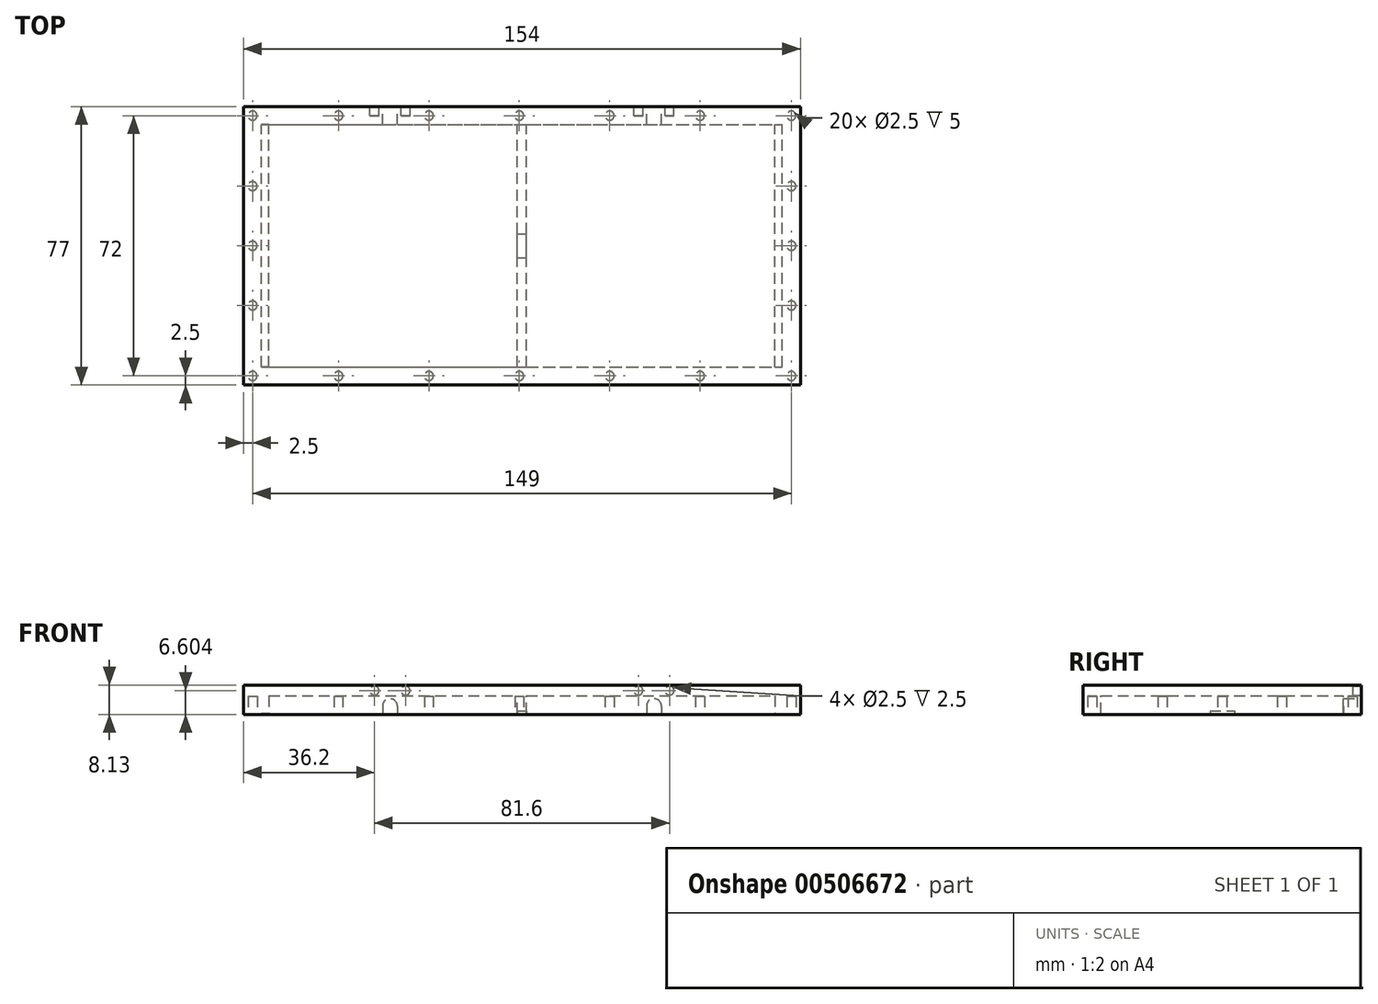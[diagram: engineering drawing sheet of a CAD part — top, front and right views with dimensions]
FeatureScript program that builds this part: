
annotation { "Feature Type Name" : "Feature", "Feature Type Description" : "" }
export const myFeature = defineFeature(function(context is Context, id is Id, definition is map)
    precondition{}
    {
        {
            var Q0;
            Q0=qCreatedBy(makeId("Top.planeOp"),FACE);
            var sketch = newSketch(context, id + "F0", { "sketchPlane" : qUnion([Q0])});
            skLineSegment(sketch, "E0.bottom", {"start": v(0, 0) * mm, "end": v(154, 0) * mm});
            skLineSegment(sketch, "E0.top", {"start": v(0, 77) * mm, "end": v(154, 77) * mm});
            skLineSegment(sketch, "E0.left", {"start": v(0, 0) * mm, "end": v(0, 77) * mm});
            skLineSegment(sketch, "E0.right", {"start": v(154, 0) * mm, "end": v(154, 77) * mm});
            skSolve(sketch);
        }
        {
            var Q0;
            Q0=qSketchRegion(id+"F0",true);
            extrude(context, id + "F1", {"entities" : qUnion([Q0]), "depth" : 8.13 * mm});
        }
        {
            var Q0;
            Q0=qCreatedBy(makeId("Top.planeOp"),FACE);
            var sketch = newSketch(context, id + "F2", { "sketchPlane" : qUnion([Q0])});
            skLineSegment(sketch, "E1.bottom", {"start": v(7, 5) * mm, "end": v(147, 5) * mm});
            skLineSegment(sketch, "E1.top", {"start": v(7, 72) * mm, "end": v(147, 72) * mm});
            skLineSegment(sketch, "E1.left", {"start": v(7, 5) * mm, "end": v(7, 72) * mm});
            skLineSegment(sketch, "E1.right", {"start": v(147, 5) * mm, "end": v(147, 72) * mm});
            skSolve(sketch);
        }
        {
            var Q0;
            Q0=makeQuery(id+"FBTdZfje9oESd4h_1.boolean.opBoolean","MERGE",FACE,{"derivedFrom":[makeQuery(id+"F1.opExtrude","CAP_FACE",FACE,{"disambiguationData":[OSD([sQuery(id+"F0.wireOp",EDGE,"E0.bottom"),sQuery(id+"F0.wireOp",EDGE,"E0.top"),sQuery(id+"F0.wireOp",EDGE,"E0.left"),sQuery(id+"F0.wireOp",EDGE,"E0.right")])],"isStart":true}),makeQuery(id+"FBTdZfje9oESd4h_1.opExtrude","SWEPT_FACE",FACE,{"disambiguationData":[OSD([sQuery(id+"Fv8mD8NBVYPvEqm_1.wireOp",EDGE,"SW5fG8um-qWP8-ISq3-XbeF-8tmbcfxiggH7.bottom")])]})]});
            var sketch = newSketch(context, id + "F3", { "sketchPlane" : qUnion([Q0])});
            skCircle(sketch, "E2", {"center": v(2.5, -2.5) * mm, "radius": 1.25 * mm});
            skSolve(sketch);
        }
        {
            var Q0;
            Q0=qSketchRegion(id+"F3",true);
            extrude(context, id + "F4", {"entities" : qUnion([Q0]), "operationType" : NewBodyOperationType.REMOVE, "oppositeDirection" : true, "depth" : 5 * mm});
        }
        {
            var Q0;
            Q0=makeQuery(id+"FBTdZfje9oESd4h_1.boolean.opBoolean","MERGE",FACE,{"derivedFrom":[makeQuery(id+"F1.opExtrude","CAP_FACE",FACE,{"disambiguationData":[OSD([sQuery(id+"F0.wireOp",EDGE,"E0.bottom"),sQuery(id+"F0.wireOp",EDGE,"E0.top"),sQuery(id+"F0.wireOp",EDGE,"E0.left"),sQuery(id+"F0.wireOp",EDGE,"E0.right")])],"isStart":true}),makeQuery(id+"FBTdZfje9oESd4h_1.opExtrude","SWEPT_FACE",FACE,{"disambiguationData":[OSD([sQuery(id+"Fv8mD8NBVYPvEqm_1.wireOp",EDGE,"SW5fG8um-qWP8-ISq3-XbeF-8tmbcfxiggH7.bottom")])]})]});
            var sketch = newSketch(context, id + "F5", { "sketchPlane" : qUnion([Q0])});
            skCircle(sketch, "E3", {"center": v(2.5, -22) * mm, "radius": 1.25 * mm});
            skSolve(sketch);
        }
        {
            var Q0;
            Q0=qSketchRegion(id+"F5",true);
            extrude(context, id + "F6", {"entities" : qUnion([Q0]), "operationType" : NewBodyOperationType.REMOVE, "oppositeDirection" : true, "depth" : 5 * mm});
        }
        {
            var Q0;
            Q0=makeQuery(id+"FBTdZfje9oESd4h_1.boolean.opBoolean","MERGE",FACE,{"derivedFrom":[makeQuery(id+"F1.opExtrude","CAP_FACE",FACE,{"disambiguationData":[OSD([sQuery(id+"F0.wireOp",EDGE,"E0.bottom"),sQuery(id+"F0.wireOp",EDGE,"E0.top"),sQuery(id+"F0.wireOp",EDGE,"E0.left"),sQuery(id+"F0.wireOp",EDGE,"E0.right")])],"isStart":true}),makeQuery(id+"FBTdZfje9oESd4h_1.opExtrude","SWEPT_FACE",FACE,{"disambiguationData":[OSD([sQuery(id+"Fv8mD8NBVYPvEqm_1.wireOp",EDGE,"SW5fG8um-qWP8-ISq3-XbeF-8tmbcfxiggH7.bottom")])]})]});
            var sketch = newSketch(context, id + "F7", { "sketchPlane" : qUnion([Q0])});
            skCircle(sketch, "E4", {"center": v(151.5, -2.5) * mm, "radius": 1.25 * mm});
            skSolve(sketch);
        }
        {
            var Q0;
            Q0=qSketchRegion(id+"F7",true);
            extrude(context, id + "F8", {"entities" : qUnion([Q0]), "operationType" : NewBodyOperationType.REMOVE, "oppositeDirection" : true, "depth" : 5 * mm});
        }
        {
            var Q0;
            Q0=makeQuery(id+"FBTdZfje9oESd4h_1.boolean.opBoolean","MERGE",FACE,{"derivedFrom":[makeQuery(id+"F1.opExtrude","CAP_FACE",FACE,{"disambiguationData":[OSD([sQuery(id+"F0.wireOp",EDGE,"E0.bottom"),sQuery(id+"F0.wireOp",EDGE,"E0.top"),sQuery(id+"F0.wireOp",EDGE,"E0.left"),sQuery(id+"F0.wireOp",EDGE,"E0.right")])],"isStart":true}),makeQuery(id+"FBTdZfje9oESd4h_1.opExtrude","SWEPT_FACE",FACE,{"disambiguationData":[OSD([sQuery(id+"Fv8mD8NBVYPvEqm_1.wireOp",EDGE,"SW5fG8um-qWP8-ISq3-XbeF-8tmbcfxiggH7.bottom")])]})]});
            var sketch = newSketch(context, id + "F9", { "sketchPlane" : qUnion([Q0])});
            skCircle(sketch, "E5", {"center": v(151.5, -22) * mm, "radius": 1.25 * mm});
            skSolve(sketch);
        }
        {
            var Q0;
            Q0=qSketchRegion(id+"F9",true);
            extrude(context, id + "F10", {"entities" : qUnion([Q0]), "operationType" : NewBodyOperationType.REMOVE, "oppositeDirection" : true, "depth" : 5 * mm});
        }
        {
            var Q0;
            Q0=makeQuery(id+"FBTdZfje9oESd4h_1.boolean.opBoolean","MERGE",FACE,{"derivedFrom":[makeQuery(id+"F1.opExtrude","CAP_FACE",FACE,{"disambiguationData":[OSD([sQuery(id+"F0.wireOp",EDGE,"E0.bottom"),sQuery(id+"F0.wireOp",EDGE,"E0.top"),sQuery(id+"F0.wireOp",EDGE,"E0.left"),sQuery(id+"F0.wireOp",EDGE,"E0.right")])],"isStart":true}),makeQuery(id+"FBTdZfje9oESd4h_1.opExtrude","SWEPT_FACE",FACE,{"disambiguationData":[OSD([sQuery(id+"Fv8mD8NBVYPvEqm_1.wireOp",EDGE,"SW5fG8um-qWP8-ISq3-XbeF-8tmbcfxiggH7.bottom")])]})]});
            var sketch = newSketch(context, id + "F11", { "sketchPlane" : qUnion([Q0])});
            skCircle(sketch, "E6", {"center": v(2.5, -38.5) * mm, "radius": 1.25 * mm});
            skSolve(sketch);
        }
        {
            var Q0;
            Q0=qSketchRegion(id+"F11",true);
            extrude(context, id + "F12", {"entities" : qUnion([Q0]), "operationType" : NewBodyOperationType.REMOVE, "oppositeDirection" : true, "depth" : 5 * mm});
        }
        {
            var Q0;
            Q0=makeQuery(id+"FBTdZfje9oESd4h_1.boolean.opBoolean","MERGE",FACE,{"derivedFrom":[makeQuery(id+"F1.opExtrude","CAP_FACE",FACE,{"disambiguationData":[OSD([sQuery(id+"F0.wireOp",EDGE,"E0.bottom"),sQuery(id+"F0.wireOp",EDGE,"E0.top"),sQuery(id+"F0.wireOp",EDGE,"E0.left"),sQuery(id+"F0.wireOp",EDGE,"E0.right")])],"isStart":true}),makeQuery(id+"FBTdZfje9oESd4h_1.opExtrude","SWEPT_FACE",FACE,{"disambiguationData":[OSD([sQuery(id+"Fv8mD8NBVYPvEqm_1.wireOp",EDGE,"SW5fG8um-qWP8-ISq3-XbeF-8tmbcfxiggH7.bottom")])]})]});
            var sketch = newSketch(context, id + "F13", { "sketchPlane" : qUnion([Q0])});
            skCircle(sketch, "E7", {"center": v(151.5, -38.5) * mm, "radius": 1.25 * mm});
            skSolve(sketch);
        }
        {
            var Q0;
            Q0=qSketchRegion(id+"F13",true);
            extrude(context, id + "F14", {"entities" : qUnion([Q0]), "operationType" : NewBodyOperationType.REMOVE, "oppositeDirection" : true, "depth" : 5 * mm});
        }
        {
            var Q0;
            Q0=makeQuery(id+"FBTdZfje9oESd4h_1.boolean.opBoolean","MERGE",FACE,{"derivedFrom":[makeQuery(id+"F1.opExtrude","CAP_FACE",FACE,{"disambiguationData":[OSD([sQuery(id+"F0.wireOp",EDGE,"E0.bottom"),sQuery(id+"F0.wireOp",EDGE,"E0.top"),sQuery(id+"F0.wireOp",EDGE,"E0.left"),sQuery(id+"F0.wireOp",EDGE,"E0.right")])],"isStart":true}),makeQuery(id+"FBTdZfje9oESd4h_1.opExtrude","SWEPT_FACE",FACE,{"disambiguationData":[OSD([sQuery(id+"Fv8mD8NBVYPvEqm_1.wireOp",EDGE,"SW5fG8um-qWP8-ISq3-XbeF-8tmbcfxiggH7.bottom")])]})]});
            var sketch = newSketch(context, id + "F15", { "sketchPlane" : qUnion([Q0])});
            skCircle(sketch, "E8", {"center": v(2.5, -55) * mm, "radius": 1.25 * mm});
            skSolve(sketch);
        }
        {
            var Q0;
            Q0=qSketchRegion(id+"F15",true);
            extrude(context, id + "F16", {"entities" : qUnion([Q0]), "operationType" : NewBodyOperationType.REMOVE, "oppositeDirection" : true, "depth" : 5 * mm});
        }
        {
            var Q0;
            Q0=makeQuery(id+"FBTdZfje9oESd4h_1.boolean.opBoolean","MERGE",FACE,{"derivedFrom":[makeQuery(id+"F1.opExtrude","CAP_FACE",FACE,{"disambiguationData":[OSD([sQuery(id+"F0.wireOp",EDGE,"E0.bottom"),sQuery(id+"F0.wireOp",EDGE,"E0.top"),sQuery(id+"F0.wireOp",EDGE,"E0.left"),sQuery(id+"F0.wireOp",EDGE,"E0.right")])],"isStart":true}),makeQuery(id+"FBTdZfje9oESd4h_1.opExtrude","SWEPT_FACE",FACE,{"disambiguationData":[OSD([sQuery(id+"Fv8mD8NBVYPvEqm_1.wireOp",EDGE,"SW5fG8um-qWP8-ISq3-XbeF-8tmbcfxiggH7.bottom")])]})]});
            var sketch = newSketch(context, id + "F17", { "sketchPlane" : qUnion([Q0])});
            skCircle(sketch, "E9", {"center": v(151.5, -55) * mm, "radius": 1.25 * mm});
            skSolve(sketch);
        }
        {
            var Q0;
            Q0=qSketchRegion(id+"F17",true);
            extrude(context, id + "F18", {"entities" : qUnion([Q0]), "operationType" : NewBodyOperationType.REMOVE, "oppositeDirection" : true, "depth" : 5 * mm});
        }
        {
            var Q0;
            Q0=makeQuery(id+"FBTdZfje9oESd4h_1.boolean.opBoolean","MERGE",FACE,{"derivedFrom":[makeQuery(id+"F1.opExtrude","CAP_FACE",FACE,{"disambiguationData":[OSD([sQuery(id+"F0.wireOp",EDGE,"E0.bottom"),sQuery(id+"F0.wireOp",EDGE,"E0.top"),sQuery(id+"F0.wireOp",EDGE,"E0.left"),sQuery(id+"F0.wireOp",EDGE,"E0.right")])],"isStart":true}),makeQuery(id+"FBTdZfje9oESd4h_1.opExtrude","SWEPT_FACE",FACE,{"disambiguationData":[OSD([sQuery(id+"Fv8mD8NBVYPvEqm_1.wireOp",EDGE,"SW5fG8um-qWP8-ISq3-XbeF-8tmbcfxiggH7.bottom")])]})]});
            var sketch = newSketch(context, id + "F19", { "sketchPlane" : qUnion([Q0])});
            skCircle(sketch, "E10", {"center": v(2.5, -74.5) * mm, "radius": 1.25 * mm});
            skSolve(sketch);
        }
        {
            var Q0;
            Q0=qSketchRegion(id+"F19",true);
            extrude(context, id + "F20", {"entities" : qUnion([Q0]), "operationType" : NewBodyOperationType.REMOVE, "oppositeDirection" : true, "depth" : 5 * mm});
        }
        {
            var Q0;
            Q0=makeQuery(id+"FBTdZfje9oESd4h_1.boolean.opBoolean","MERGE",FACE,{"derivedFrom":[makeQuery(id+"F1.opExtrude","CAP_FACE",FACE,{"disambiguationData":[OSD([sQuery(id+"F0.wireOp",EDGE,"E0.bottom"),sQuery(id+"F0.wireOp",EDGE,"E0.top"),sQuery(id+"F0.wireOp",EDGE,"E0.left"),sQuery(id+"F0.wireOp",EDGE,"E0.right")])],"isStart":true}),makeQuery(id+"FBTdZfje9oESd4h_1.opExtrude","SWEPT_FACE",FACE,{"disambiguationData":[OSD([sQuery(id+"Fv8mD8NBVYPvEqm_1.wireOp",EDGE,"SW5fG8um-qWP8-ISq3-XbeF-8tmbcfxiggH7.bottom")])]})]});
            var sketch = newSketch(context, id + "F21", { "sketchPlane" : qUnion([Q0])});
            skCircle(sketch, "E11", {"center": v(151.5, -74.5) * mm, "radius": 1.25 * mm});
            skSolve(sketch);
        }
        {
            var Q0;
            Q0=qSketchRegion(id+"F21",true);
            extrude(context, id + "F22", {"entities" : qUnion([Q0]), "operationType" : NewBodyOperationType.REMOVE, "oppositeDirection" : true, "depth" : 5 * mm});
        }
        {
            var Q0;
            Q0=makeQuery(id+"FBTdZfje9oESd4h_1.boolean.opBoolean","MERGE",FACE,{"derivedFrom":[makeQuery(id+"F1.opExtrude","CAP_FACE",FACE,{"disambiguationData":[OSD([sQuery(id+"F0.wireOp",EDGE,"E0.bottom"),sQuery(id+"F0.wireOp",EDGE,"E0.top"),sQuery(id+"F0.wireOp",EDGE,"E0.left"),sQuery(id+"F0.wireOp",EDGE,"E0.right")])],"isStart":true}),makeQuery(id+"FBTdZfje9oESd4h_1.opExtrude","SWEPT_FACE",FACE,{"disambiguationData":[OSD([sQuery(id+"Fv8mD8NBVYPvEqm_1.wireOp",EDGE,"SW5fG8um-qWP8-ISq3-XbeF-8tmbcfxiggH7.bottom")])]})]});
            var sketch = newSketch(context, id + "F23", { "sketchPlane" : qUnion([Q0])});
            skCircle(sketch, "E12", {"center": v(26.25, -2.5) * mm, "radius": 1.25 * mm});
            skSolve(sketch);
        }
        {
            var Q0;
            Q0=qSketchRegion(id+"F23",true);
            extrude(context, id + "F24", {"entities" : qUnion([Q0]), "operationType" : NewBodyOperationType.REMOVE, "oppositeDirection" : true, "depth" : 5 * mm});
        }
        {
            var Q0;
            Q0=makeQuery(id+"FBTdZfje9oESd4h_1.boolean.opBoolean","MERGE",FACE,{"derivedFrom":[makeQuery(id+"F1.opExtrude","CAP_FACE",FACE,{"disambiguationData":[OSD([sQuery(id+"F0.wireOp",EDGE,"E0.bottom"),sQuery(id+"F0.wireOp",EDGE,"E0.top"),sQuery(id+"F0.wireOp",EDGE,"E0.left"),sQuery(id+"F0.wireOp",EDGE,"E0.right")])],"isStart":true}),makeQuery(id+"FBTdZfje9oESd4h_1.opExtrude","SWEPT_FACE",FACE,{"disambiguationData":[OSD([sQuery(id+"Fv8mD8NBVYPvEqm_1.wireOp",EDGE,"SW5fG8um-qWP8-ISq3-XbeF-8tmbcfxiggH7.bottom")])]})]});
            var sketch = newSketch(context, id + "F25", { "sketchPlane" : qUnion([Q0])});
            skCircle(sketch, "E13", {"center": v(26.25, -74.5) * mm, "radius": 1.25 * mm});
            skSolve(sketch);
        }
        {
            var Q0;
            Q0=qSketchRegion(id+"F25",true);
            extrude(context, id + "F26", {"entities" : qUnion([Q0]), "operationType" : NewBodyOperationType.REMOVE, "oppositeDirection" : true, "depth" : 5 * mm});
        }
        {
            var Q0;
            Q0=makeQuery(id+"FBTdZfje9oESd4h_1.boolean.opBoolean","MERGE",FACE,{"derivedFrom":[makeQuery(id+"F1.opExtrude","CAP_FACE",FACE,{"disambiguationData":[OSD([sQuery(id+"F0.wireOp",EDGE,"E0.bottom"),sQuery(id+"F0.wireOp",EDGE,"E0.top"),sQuery(id+"F0.wireOp",EDGE,"E0.left"),sQuery(id+"F0.wireOp",EDGE,"E0.right")])],"isStart":true}),makeQuery(id+"FBTdZfje9oESd4h_1.opExtrude","SWEPT_FACE",FACE,{"disambiguationData":[OSD([sQuery(id+"Fv8mD8NBVYPvEqm_1.wireOp",EDGE,"SW5fG8um-qWP8-ISq3-XbeF-8tmbcfxiggH7.bottom")])]})]});
            var sketch = newSketch(context, id + "F27", { "sketchPlane" : qUnion([Q0])});
            skCircle(sketch, "E14", {"center": v(51.25, -2.5) * mm, "radius": 1.25 * mm});
            skSolve(sketch);
        }
        {
            var Q0;
            Q0=qSketchRegion(id+"F27",true);
            extrude(context, id + "F28", {"entities" : qUnion([Q0]), "operationType" : NewBodyOperationType.REMOVE, "oppositeDirection" : true, "depth" : 5 * mm});
        }
        {
            var Q0;
            Q0=makeQuery(id+"FBTdZfje9oESd4h_1.boolean.opBoolean","MERGE",FACE,{"derivedFrom":[makeQuery(id+"F1.opExtrude","CAP_FACE",FACE,{"disambiguationData":[OSD([sQuery(id+"F0.wireOp",EDGE,"E0.bottom"),sQuery(id+"F0.wireOp",EDGE,"E0.top"),sQuery(id+"F0.wireOp",EDGE,"E0.left"),sQuery(id+"F0.wireOp",EDGE,"E0.right")])],"isStart":true}),makeQuery(id+"FBTdZfje9oESd4h_1.opExtrude","SWEPT_FACE",FACE,{"disambiguationData":[OSD([sQuery(id+"Fv8mD8NBVYPvEqm_1.wireOp",EDGE,"SW5fG8um-qWP8-ISq3-XbeF-8tmbcfxiggH7.bottom")])]})]});
            var sketch = newSketch(context, id + "F29", { "sketchPlane" : qUnion([Q0])});
            skCircle(sketch, "E15", {"center": v(76.25, -2.5) * mm, "radius": 1.25 * mm});
            skSolve(sketch);
        }
        {
            var Q0;
            Q0=qSketchRegion(id+"F29",true);
            extrude(context, id + "F30", {"entities" : qUnion([Q0]), "operationType" : NewBodyOperationType.REMOVE, "oppositeDirection" : true, "depth" : 5 * mm});
        }
        {
            var Q0;
            Q0=makeQuery(id+"FBTdZfje9oESd4h_1.boolean.opBoolean","MERGE",FACE,{"derivedFrom":[makeQuery(id+"F1.opExtrude","CAP_FACE",FACE,{"disambiguationData":[OSD([sQuery(id+"F0.wireOp",EDGE,"E0.bottom"),sQuery(id+"F0.wireOp",EDGE,"E0.top"),sQuery(id+"F0.wireOp",EDGE,"E0.left"),sQuery(id+"F0.wireOp",EDGE,"E0.right")])],"isStart":true}),makeQuery(id+"FBTdZfje9oESd4h_1.opExtrude","SWEPT_FACE",FACE,{"disambiguationData":[OSD([sQuery(id+"Fv8mD8NBVYPvEqm_1.wireOp",EDGE,"SW5fG8um-qWP8-ISq3-XbeF-8tmbcfxiggH7.bottom")])]})]});
            var sketch = newSketch(context, id + "F31", { "sketchPlane" : qUnion([Q0])});
            skCircle(sketch, "E16", {"center": v(51.25, -74.5) * mm, "radius": 1.25 * mm});
            skSolve(sketch);
        }
        {
            var Q0;
            Q0=qSketchRegion(id+"F31",true);
            extrude(context, id + "F32", {"entities" : qUnion([Q0]), "operationType" : NewBodyOperationType.REMOVE, "oppositeDirection" : true, "depth" : 5 * mm});
        }
        {
            var Q0;
            Q0=makeQuery(id+"FBTdZfje9oESd4h_1.boolean.opBoolean","MERGE",FACE,{"derivedFrom":[makeQuery(id+"F1.opExtrude","CAP_FACE",FACE,{"disambiguationData":[OSD([sQuery(id+"F0.wireOp",EDGE,"E0.bottom"),sQuery(id+"F0.wireOp",EDGE,"E0.top"),sQuery(id+"F0.wireOp",EDGE,"E0.left"),sQuery(id+"F0.wireOp",EDGE,"E0.right")])],"isStart":true}),makeQuery(id+"FBTdZfje9oESd4h_1.opExtrude","SWEPT_FACE",FACE,{"disambiguationData":[OSD([sQuery(id+"Fv8mD8NBVYPvEqm_1.wireOp",EDGE,"SW5fG8um-qWP8-ISq3-XbeF-8tmbcfxiggH7.bottom")])]})]});
            var sketch = newSketch(context, id + "F33", { "sketchPlane" : qUnion([Q0])});
            skCircle(sketch, "E17", {"center": v(101.25, -2.5) * mm, "radius": 1.25 * mm});
            skSolve(sketch);
        }
        {
            var Q0;
            Q0=qSketchRegion(id+"F33",true);
            extrude(context, id + "F34", {"entities" : qUnion([Q0]), "operationType" : NewBodyOperationType.REMOVE, "oppositeDirection" : true, "depth" : 5 * mm});
        }
        {
            var Q0;
            Q0=makeQuery(id+"FBTdZfje9oESd4h_1.boolean.opBoolean","MERGE",FACE,{"derivedFrom":[makeQuery(id+"F1.opExtrude","CAP_FACE",FACE,{"disambiguationData":[OSD([sQuery(id+"F0.wireOp",EDGE,"E0.bottom"),sQuery(id+"F0.wireOp",EDGE,"E0.top"),sQuery(id+"F0.wireOp",EDGE,"E0.left"),sQuery(id+"F0.wireOp",EDGE,"E0.right")])],"isStart":true}),makeQuery(id+"FBTdZfje9oESd4h_1.opExtrude","SWEPT_FACE",FACE,{"disambiguationData":[OSD([sQuery(id+"Fv8mD8NBVYPvEqm_1.wireOp",EDGE,"SW5fG8um-qWP8-ISq3-XbeF-8tmbcfxiggH7.bottom")])]})]});
            var sketch = newSketch(context, id + "F35", { "sketchPlane" : qUnion([Q0])});
            skCircle(sketch, "E18", {"center": v(76.25, -74.5) * mm, "radius": 1.25 * mm});
            skSolve(sketch);
        }
        {
            var Q0;
            Q0=qSketchRegion(id+"F35",true);
            extrude(context, id + "F36", {"entities" : qUnion([Q0]), "operationType" : NewBodyOperationType.REMOVE, "oppositeDirection" : true, "depth" : 5 * mm});
        }
        {
            var Q0;
            Q0=makeQuery(id+"FBTdZfje9oESd4h_1.boolean.opBoolean","MERGE",FACE,{"derivedFrom":[makeQuery(id+"F1.opExtrude","CAP_FACE",FACE,{"disambiguationData":[OSD([sQuery(id+"F0.wireOp",EDGE,"E0.bottom"),sQuery(id+"F0.wireOp",EDGE,"E0.top"),sQuery(id+"F0.wireOp",EDGE,"E0.left"),sQuery(id+"F0.wireOp",EDGE,"E0.right")])],"isStart":true}),makeQuery(id+"FBTdZfje9oESd4h_1.opExtrude","SWEPT_FACE",FACE,{"disambiguationData":[OSD([sQuery(id+"Fv8mD8NBVYPvEqm_1.wireOp",EDGE,"SW5fG8um-qWP8-ISq3-XbeF-8tmbcfxiggH7.bottom")])]})]});
            var sketch = newSketch(context, id + "F37", { "sketchPlane" : qUnion([Q0])});
            skCircle(sketch, "E19", {"center": v(126.25, -2.5) * mm, "radius": 1.25 * mm});
            skSolve(sketch);
        }
        {
            var Q0;
            Q0=qSketchRegion(id+"F37",true);
            extrude(context, id + "F38", {"entities" : qUnion([Q0]), "operationType" : NewBodyOperationType.REMOVE, "oppositeDirection" : true, "depth" : 5 * mm});
        }
        {
            var Q0;
            Q0=makeQuery(id+"FBTdZfje9oESd4h_1.boolean.opBoolean","MERGE",FACE,{"derivedFrom":[makeQuery(id+"F1.opExtrude","CAP_FACE",FACE,{"disambiguationData":[OSD([sQuery(id+"F0.wireOp",EDGE,"E0.bottom"),sQuery(id+"F0.wireOp",EDGE,"E0.top"),sQuery(id+"F0.wireOp",EDGE,"E0.left"),sQuery(id+"F0.wireOp",EDGE,"E0.right")])],"isStart":true}),makeQuery(id+"FBTdZfje9oESd4h_1.opExtrude","SWEPT_FACE",FACE,{"disambiguationData":[OSD([sQuery(id+"Fv8mD8NBVYPvEqm_1.wireOp",EDGE,"SW5fG8um-qWP8-ISq3-XbeF-8tmbcfxiggH7.bottom")])]})]});
            var sketch = newSketch(context, id + "F39", { "sketchPlane" : qUnion([Q0])});
            skCircle(sketch, "E20", {"center": v(101.25, -74.5) * mm, "radius": 1.25 * mm});
            skSolve(sketch);
        }
        {
            var Q0;
            Q0=qSketchRegion(id+"F39",true);
            extrude(context, id + "F40", {"entities" : qUnion([Q0]), "operationType" : NewBodyOperationType.REMOVE, "oppositeDirection" : true, "depth" : 5 * mm});
        }
        {
            var Q0;
            Q0=makeQuery(id+"FBTdZfje9oESd4h_1.boolean.opBoolean","MERGE",FACE,{"derivedFrom":[makeQuery(id+"F1.opExtrude","CAP_FACE",FACE,{"disambiguationData":[OSD([sQuery(id+"F0.wireOp",EDGE,"E0.bottom"),sQuery(id+"F0.wireOp",EDGE,"E0.top"),sQuery(id+"F0.wireOp",EDGE,"E0.left"),sQuery(id+"F0.wireOp",EDGE,"E0.right")])],"isStart":true}),makeQuery(id+"FBTdZfje9oESd4h_1.opExtrude","SWEPT_FACE",FACE,{"disambiguationData":[OSD([sQuery(id+"Fv8mD8NBVYPvEqm_1.wireOp",EDGE,"SW5fG8um-qWP8-ISq3-XbeF-8tmbcfxiggH7.bottom")])]})]});
            var sketch = newSketch(context, id + "F41", { "sketchPlane" : qUnion([Q0])});
            skCircle(sketch, "E21", {"center": v(126.25, -74.5) * mm, "radius": 1.25 * mm});
            skSolve(sketch);
        }
        {
            var Q0;
            Q0=qSketchRegion(id+"F41",true);
            extrude(context, id + "F42", {"entities" : qUnion([Q0]), "operationType" : NewBodyOperationType.REMOVE, "oppositeDirection" : true, "depth" : 5 * mm});
        }
        {
            var Q0;
            Q0=qSketchRegion(id+"F2",true);
            extrude(context, id + "F43", {"entities" : qUnion([Q0]), "operationType" : NewBodyOperationType.REMOVE, "depth" : 5.13 * mm});
        }
        {
            var Q0;
            Q0=makeQuery(id+"F43.boolean.opBoolean","COPY",FACE,{"derivedFrom":makeQuery(id+"F43.opExtrude","CAP_FACE",FACE,{"disambiguationData":[OSD([sQuery(id+"F2.wireOp",EDGE,"E1.bottom"),sQuery(id+"F2.wireOp",EDGE,"E1.top"),sQuery(id+"F2.wireOp",EDGE,"E1.left"),sQuery(id+"F2.wireOp",EDGE,"E1.right")])],"isStart":false})});
            var sketch = newSketch(context, id + "F44", { "sketchPlane" : qUnion([Q0])});
            skLineSegment(sketch, "E22.bottom", {"start": v(75.75, -5) * mm, "end": v(78.25, -5) * mm});
            skLineSegment(sketch, "E22.top", {"start": v(75.75, -72) * mm, "end": v(78.25, -72) * mm});
            skLineSegment(sketch, "E22.left", {"start": v(75.75, -5) * mm, "end": v(75.75, -72) * mm});
            skLineSegment(sketch, "E22.right", {"start": v(78.25, -5) * mm, "end": v(78.25, -72) * mm});
            skSolve(sketch);
        }
        {
            var Q0;
            Q0=makeQuery(id+"F1.opExtrude","CAP_FACE",FACE,{"disambiguationData":[OSD([sQuery(id+"F0.wireOp",EDGE,"E0.bottom"),sQuery(id+"F0.wireOp",EDGE,"E0.top"),sQuery(id+"F0.wireOp",EDGE,"E0.left"),sQuery(id+"F0.wireOp",EDGE,"E0.right")])],"isStart":true});
            var sketch = newSketch(context, id + "F45", { "sketchPlane" : qUnion([Q0])});
            skLineSegment(sketch, "E23.bottom", {"start": v(7, -5) * mm, "end": v(5, -5) * mm});
            skLineSegment(sketch, "E23.top", {"start": v(7, -72) * mm, "end": v(5, -72) * mm});
            skLineSegment(sketch, "E23.left", {"start": v(7, -5) * mm, "end": v(7, -72) * mm});
            skLineSegment(sketch, "E23.right", {"start": v(5, -5) * mm, "end": v(5, -72) * mm});
            skSolve(sketch);
        }
        {
            var Q0;
            Q0=qSketchRegion(id+"F45",true);
            extrude(context, id + "F46", {"entities" : qUnion([Q0]), "operationType" : NewBodyOperationType.REMOVE, "oppositeDirection" : true, "depth" : 0.25 * mm});
        }
        {
            var Q0;
            Q0=makeQuery(id+"F1.opExtrude","CAP_FACE",FACE,{"disambiguationData":[OSD([sQuery(id+"F0.wireOp",EDGE,"E0.bottom"),sQuery(id+"F0.wireOp",EDGE,"E0.top"),sQuery(id+"F0.wireOp",EDGE,"E0.left"),sQuery(id+"F0.wireOp",EDGE,"E0.right")])],"isStart":true});
            var sketch = newSketch(context, id + "F47", { "sketchPlane" : qUnion([Q0])});
            skLineSegment(sketch, "E24.bottom", {"start": v(147, -5) * mm, "end": v(149, -5) * mm});
            skLineSegment(sketch, "E24.top", {"start": v(147, -72) * mm, "end": v(149, -72) * mm});
            skLineSegment(sketch, "E24.left", {"start": v(147, -5) * mm, "end": v(147, -72) * mm});
            skLineSegment(sketch, "E24.right", {"start": v(149, -5) * mm, "end": v(149, -72) * mm});
            skSolve(sketch);
        }
        {
            var Q0;
            Q0=qSketchRegion(id+"F47",true);
            extrude(context, id + "F48", {"entities" : qUnion([Q0]), "operationType" : NewBodyOperationType.REMOVE, "oppositeDirection" : true, "depth" : 0.25 * mm});
        }
        {
            var Q0;
            Q0=makeQuery(id+"F1.opExtrude","SWEPT_FACE",FACE,{"disambiguationData":[OSD([sQuery(id+"F0.wireOp",EDGE,"E0.top")])]});
            var sketch = newSketch(context, id + "F49", { "sketchPlane" : qUnion([Q0])});
            skCircle(sketch, "E25", {"center": v(-40.5, 2.3) * mm, "radius": 2.05 * mm});
            skSolve(sketch);
        }
        {
            var Q0;
            Q0=qSketchRegion(id+"F49",true);
            extrude(context, id + "F50", {"entities" : qUnion([Q0]), "operationType" : NewBodyOperationType.REMOVE, "oppositeDirection" : true, "depth" : 5 * mm});
        }
        {
            var Q0;
            Q0=makeQuery(id+"F1.opExtrude","SWEPT_FACE",FACE,{"disambiguationData":[OSD([sQuery(id+"F0.wireOp",EDGE,"E0.top")])]});
            var sketch = newSketch(context, id + "F51", { "sketchPlane" : qUnion([Q0])});
            skCircle(sketch, "E26", {"center": v(-113.5, 2.3) * mm, "radius": 2.05 * mm});
            skSolve(sketch);
        }
        {
            var Q0;
            Q0=qSketchRegion(id+"F51",true);
            extrude(context, id + "F52", {"entities" : qUnion([Q0]), "operationType" : NewBodyOperationType.REMOVE, "oppositeDirection" : true, "depth" : 5 * mm});
        }
        {
            var Q0;
            Q0=makeQuery(id+"F1.opExtrude","SWEPT_FACE",FACE,{"disambiguationData":[OSD([sQuery(id+"F0.wireOp",EDGE,"E0.top")])]});
            var sketch = newSketch(context, id + "F53", { "sketchPlane" : qUnion([Q0])});
            skLineSegment(sketch, "E27.bottom", {"start": v(-115.55, 2.3) * mm, "end": v(-111.45, 2.3) * mm});
            skLineSegment(sketch, "E27.top", {"start": v(-115.55, 0) * mm, "end": v(-111.45, 0) * mm});
            skLineSegment(sketch, "E27.left", {"start": v(-115.55, 2.3) * mm, "end": v(-115.55, 0) * mm});
            skLineSegment(sketch, "E27.right", {"start": v(-111.45, 2.3) * mm, "end": v(-111.45, 0) * mm});
            skSolve(sketch);
        }
        {
            var Q0;
            Q0=qSketchRegion(id+"F53",true);
            extrude(context, id + "F54", {"entities" : qUnion([Q0]), "operationType" : NewBodyOperationType.REMOVE, "oppositeDirection" : true, "depth" : 5 * mm});
        }
        {
            var Q0;
            Q0=makeQuery(id+"F1.opExtrude","SWEPT_FACE",FACE,{"disambiguationData":[OSD([sQuery(id+"F0.wireOp",EDGE,"E0.top")])]});
            var sketch = newSketch(context, id + "F55", { "sketchPlane" : qUnion([Q0])});
            skLineSegment(sketch, "E28.bottom", {"start": v(-42.55, 2.3) * mm, "end": v(-38.45, 2.3) * mm});
            skLineSegment(sketch, "E28.top", {"start": v(-42.55, 0) * mm, "end": v(-38.45, 0) * mm});
            skLineSegment(sketch, "E28.left", {"start": v(-42.55, 2.3) * mm, "end": v(-42.55, 0) * mm});
            skLineSegment(sketch, "E28.right", {"start": v(-38.45, 2.3) * mm, "end": v(-38.45, 0) * mm});
            skSolve(sketch);
        }
        {
            var Q0;
            Q0=qSketchRegion(id+"F55",true);
            extrude(context, id + "F56", {"entities" : qUnion([Q0]), "operationType" : NewBodyOperationType.REMOVE, "oppositeDirection" : true, "depth" : 5 * mm});
        }
        {
            var Q0;
            Q0=makeQuery(id+"F1.opExtrude","SWEPT_FACE",FACE,{"disambiguationData":[OSD([sQuery(id+"F0.wireOp",EDGE,"E0.top")])]});
            var sketch = newSketch(context, id + "F57", { "sketchPlane" : qUnion([Q0])});
            skCircle(sketch, "E29", {"center": v(-36.2, 6.6) * mm, "radius": 1.25 * mm});
            skCircle(sketch, "E30", {"center": v(-44.8, 6.6) * mm, "radius": 1.25 * mm});
            skCircle(sketch, "E31", {"center": v(-117.8, 6.6) * mm, "radius": 1.25 * mm});
            skCircle(sketch, "E32", {"center": v(-109.2, 6.6) * mm, "radius": 1.25 * mm});
            skSolve(sketch);
        }
        {
            var Q0;
            Q0=qSketchRegion(id+"F57",true);
            extrude(context, id + "F58", {"entities" : qUnion([Q0]), "operationType" : NewBodyOperationType.REMOVE, "oppositeDirection" : true, "depth" : 2.5 * mm});
        }
        {
            var Q0;
            Q0 = qSketchRegion(id + "F44", true);
            extrude(context, id + "F59", {"entities" : qUnion([Q0]), "operationType" : NewBodyOperationType.ADD, "depth" : 4.87 * mm});
        }
        {
            var Q0;
            Q0=makeQuery(id+"F59.opExtrude","CAP_FACE",FACE,{"disambiguationData":[OSD([sQuery(id+"F44.wireOp",EDGE,"E22.bottom"),sQuery(id+"F44.wireOp",EDGE,"E22.top"),sQuery(id+"F44.wireOp",EDGE,"E22.left"),sQuery(id+"F44.wireOp",EDGE,"E22.right")])],"isStart":false});
            var sketch = newSketch(context, id + "F60", { "sketchPlane" : qUnion([Q0])});
            skLineSegment(sketch, "E33.bottom", {"start": v(75.75, -35.15) * mm, "end": v(78.25, -35.15) * mm});
            skLineSegment(sketch, "E33.top", {"start": v(75.75, -41.85) * mm, "end": v(78.25, -41.85) * mm});
            skLineSegment(sketch, "E33.left", {"start": v(75.75, -35.15) * mm, "end": v(75.75, -41.85) * mm});
            skLineSegment(sketch, "E33.right", {"start": v(78.25, -35.15) * mm, "end": v(78.25, -41.85) * mm});
            skSolve(sketch);
        }
        {
            var Q0;
            Q0=makeQuery(id+"F60.imprint","IMPRINT",FACE,{"disambiguationData":[TD([[makeQuery(id+"F60.imprint","IMPRINT",EDGE,{"derivedFrom":sQuery(id+"F60.wireOp",EDGE,"E33.bottom")}),-1.0]])]});
            extrude(context, id + "F61", {"entities" : qUnion([Q0]), "operationType" : NewBodyOperationType.REMOVE, "oppositeDirection" : true, "depth" : 0.72 * mm});
        }
    });
